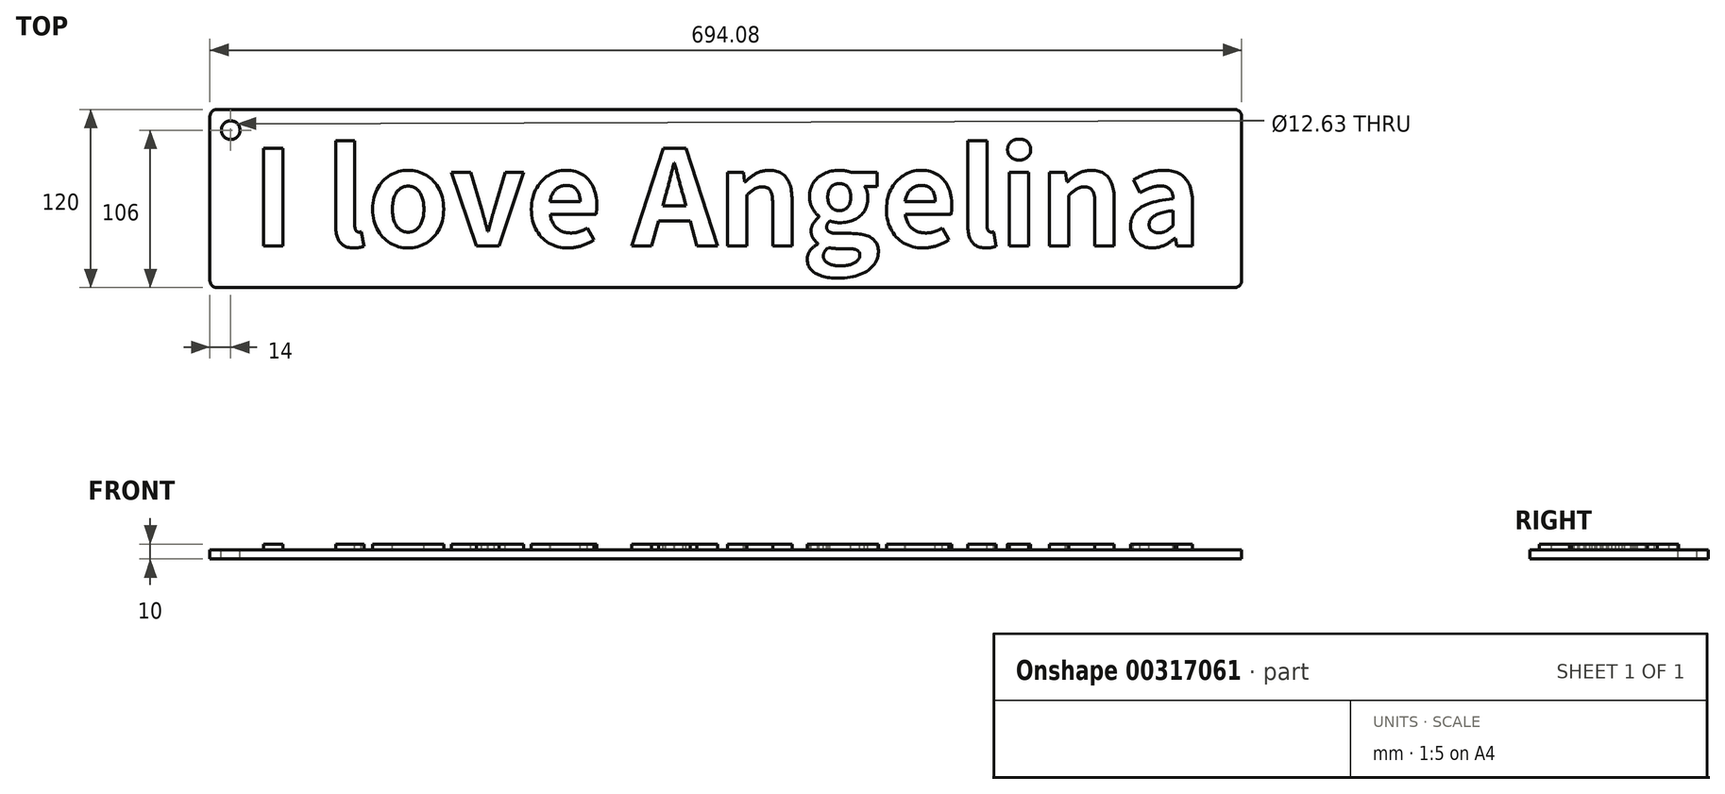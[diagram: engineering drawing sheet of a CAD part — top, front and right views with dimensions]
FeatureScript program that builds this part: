
annotation { "Feature Type Name" : "Feature", "Feature Type Description" : "" }
export const myFeature = defineFeature(function(context is Context, id is Id, definition is map)
    precondition{}
    {
        {
            var Q0;
            Q0=qCreatedBy(makeId("Top.planeOp"),FACE);
            var sketch = newSketch(context, id + "F0", { "sketchPlane" : qUnion([Q0])});
            skText(sketch, "E0", { "text": "I love Angelina\n", "fontName": "NotoSansCJKkr-Bold.otf"});
            skLineSegment(sketch, "E1.bottom", {"start": v(-23, -28) * mm, "end": v(661.08, -28) * mm});
            skLineSegment(sketch, "E1.top", {"start": v(-23, 92) * mm, "end": v(661.08, 92) * mm});
            skLineSegment(sketch, "E1.left", {"start": v(-28, -23) * mm, "end": v(-28, 87) * mm});
            skLineSegment(sketch, "E1.right", {"start": v(666.08, -23) * mm, "end": v(666.08, 87) * mm});
            skLineSegment(sketch, "E2", {"start": v(0, 64) * mm, "end": v(-28, 92) * mm});
            skLineSegment(sketch, "E3", {"start": v(-28, -28) * mm, "end": v(0, 0) * mm});
            skLineSegment(sketch, "E4", {"start": v(666.08, -28) * mm, "end": v(638.08, 0) * mm});
            skLineSegment(sketch, "E5", {"start": v(0, 64) * mm, "end": v(0, 92) * mm});
            skLineSegment(sketch, "E6", {"start": v(0, 0) * mm, "end": v(0, -28) * mm});
            skLineSegment(sketch, "E7", {"start": v(0, 64) * mm, "end": v(-28, 64) * mm});
            skPoint(sketch, "E8.visualSharp", {"position": v(-28, 92) * mm});
            skArc(sketch, "E8.filletArc", {"start": v(-23, 92) * mm, "mid": v(-26.54, 90.54) * mm, "end": v(-28, 87) * mm});
            skPoint(sketch, "E9.visualSharp", {"position": v(-28, -28) * mm});
            skArc(sketch, "E9.filletArc", {"start": v(-28, -23) * mm, "mid": v(-26.54, -26.54) * mm, "end": v(-23, -28) * mm});
            skPoint(sketch, "E10.visualSharp", {"position": v(666.08, -28) * mm});
            skArc(sketch, "E10.filletArc", {"start": v(661.08, -28) * mm, "mid": v(664.62, -26.54) * mm, "end": v(666.08, -23) * mm});
            skPoint(sketch, "E11.visualSharp", {"position": v(666.08, 92) * mm});
            skArc(sketch, "E11.filletArc", {"start": v(666.08, 87) * mm, "mid": v(664.62, 90.54) * mm, "end": v(661.08, 92) * mm});
            skPoint(sketch, "E12", {"position": v(-14, 78) * mm});
            skCircle(sketch, "E13", {"center": v(-14, 78) * mm, "radius": 6.31 * mm});
            const initialGuessF0  = {"E0": [0, 0, 1, 0, 0.064]};
            skSetInitialGuess(sketch, initialGuessF0);
            skSolve(sketch);
        }
        {
            var Q0;
            Q0 = qSketchRegion(id + "F0", true);
            var Q1;
            Q1=makeQuery(id+"F0.imprint","IMPRINT",FACE,{"disambiguationData":[TD([[makeQuery(id+"F0.imprint","IMPRINT",EDGE,{"derivedFrom":sQuery(id+"F0.wireOp",EDGE,"E0.sketch_text.stroke-12")}),1.0]])]});
            var Q2;
            Q2=makeQuery(id+"F0.imprint","IMPRINT",FACE,{"disambiguationData":[TD([[makeQuery(id+"F0.imprint","IMPRINT",EDGE,{"derivedFrom":sQuery(id+"F0.wireOp",EDGE,"E0.sketch_text.stroke-0")}),-1.0]])]});
            var Q3;
            Q3=makeQuery(id+"F0.imprint","IMPRINT",FACE,{"disambiguationData":[TD([[makeQuery(id+"F0.imprint","IMPRINT",EDGE,{"derivedFrom":sQuery(id+"F0.wireOp",EDGE,"E0.sketch_text.stroke-69")}),1.0]])]});
            var Q4;
            Q4=makeQuery(id+"F0.imprint","IMPRINT",FACE,{"disambiguationData":[TD([[makeQuery(id+"F0.imprint","IMPRINT",EDGE,{"derivedFrom":sQuery(id+"F0.wireOp",EDGE,"E0.sketch_text.stroke-123")}),1.0]])]});
            var Q5;
            Q5=makeQuery(id+"F0.imprint","IMPRINT",FACE,{"disambiguationData":[TD([[makeQuery(id+"F0.imprint","IMPRINT",EDGE,{"derivedFrom":sQuery(id+"F0.wireOp",EDGE,"E0.sketch_text.stroke-119")}),1.0]])]});
            var Q6;
            Q6=makeQuery(id+"F0.imprint","IMPRINT",FACE,{"disambiguationData":[TD([[makeQuery(id+"F0.imprint","IMPRINT",EDGE,{"derivedFrom":sQuery(id+"F0.wireOp",EDGE,"E0.sketch_text.stroke-108")}),-1.0]])]});
            var Q7;
            Q7=makeQuery(id+"F0.imprint","IMPRINT",FACE,{"disambiguationData":[TD([[makeQuery(id+"F0.imprint","IMPRINT",EDGE,{"derivedFrom":sQuery(id+"F0.wireOp",EDGE,"E0.sketch_text.stroke-93")}),-1.0]])]});
            var Q8;
            Q8=makeQuery(id+"F0.imprint","IMPRINT",FACE,{"disambiguationData":[TD([[makeQuery(id+"F0.imprint","IMPRINT",EDGE,{"derivedFrom":sQuery(id+"F0.wireOp",EDGE,"E0.sketch_text.stroke-89")}),-1.0]])]});
            var Q9;
            Q9=makeQuery(id+"F0.imprint","IMPRINT",FACE,{"disambiguationData":[TD([[makeQuery(id+"F0.imprint","IMPRINT",EDGE,{"derivedFrom":sQuery(id+"F0.wireOp",EDGE,"E0.sketch_text.stroke-56")}),1.0]])]});
            var Q10;
            Q10=makeQuery(id+"F0.imprint","IMPRINT",FACE,{"disambiguationData":[TD([[makeQuery(id+"F0.imprint","IMPRINT",EDGE,{"derivedFrom":sQuery(id+"F0.wireOp",EDGE,"E0.sketch_text.stroke-42")}),-1.0]])]});
            var Q11;
            Q11=makeQuery(id+"F0.imprint","IMPRINT",FACE,{"disambiguationData":[TD([[makeQuery(id+"F0.imprint","IMPRINT",EDGE,{"derivedFrom":sQuery(id+"F0.wireOp",EDGE,"E0.sketch_text.stroke-42")}),1.0]])]});
            var Q12;
            Q12=makeQuery(id+"F0.imprint","IMPRINT",FACE,{"disambiguationData":[TD([[makeQuery(id+"F0.imprint","IMPRINT",EDGE,{"derivedFrom":sQuery(id+"F0.wireOp",EDGE,"E0.sketch_text.stroke-39")}),-1.0]])]});
            var Q13;
            Q13=makeQuery(id+"F0.imprint","IMPRINT",FACE,{"disambiguationData":[TD([[makeQuery(id+"F0.imprint","IMPRINT",EDGE,{"derivedFrom":sQuery(id+"F0.wireOp",EDGE,"E0.sketch_text.stroke-20")}),1.0]])]});
            var Q14;
            Q14=makeQuery(id+"F0.imprint","IMPRINT",FACE,{"disambiguationData":[TD([[makeQuery(id+"F0.imprint","IMPRINT",EDGE,{"derivedFrom":sQuery(id+"F0.wireOp",EDGE,"E0.sketch_text.stroke-16")}),-1.0]])]});
            var Q15;
            Q15=makeQuery(id+"F0.imprint","IMPRINT",FACE,{"disambiguationData":[TD([[makeQuery(id+"F0.imprint","IMPRINT",EDGE,{"derivedFrom":sQuery(id+"F0.wireOp",EDGE,"E0.sketch_text.stroke-4")}),1.0]])]});
            var Q16;
            Q16=makeQuery(id+"F0.imprint","IMPRINT",FACE,{"disambiguationData":[TD([[makeQuery(id+"F0.imprint","IMPRINT",EDGE,{"derivedFrom":sQuery(id+"F0.wireOp",EDGE,"E0.sketch_text.stroke-0")}),1.0]])]});
            var Q17;
            Q17=makeQuery(id+"F0.imprint","IMPRINT",FACE,{"disambiguationData":[TD([[makeQuery(id+"F0.imprint","IMPRINT",EDGE,{"derivedFrom":sQuery(id+"F0.wireOp",EDGE,"E0.sketch_text.stroke-152")}),-1.0]])]});
            var Q18;
            Q18=makeQuery(id+"F0.imprint","IMPRINT",FACE,{"disambiguationData":[TD([[makeQuery(id+"F0.imprint","IMPRINT",EDGE,{"derivedFrom":sQuery(id+"F0.wireOp",EDGE,"E0.sketch_text.stroke-127")}),1.0]])]});
            var Q19;
            {var subQ3=sQuery(id+"F0.wireOp",EDGE,"E6");Q19=makeQuery(id+"F0.imprint","IMPRINT",FACE,{"disambiguationData":[TD([[makeQuery(id+"F0.imprint","IMPRINT",EDGE,{"derivedFrom":subQ3}),-1.0]])]});}
            var Q20;
            {var subQ3=sQuery(id+"F0.wireOp",EDGE,"E7");Q20=makeQuery(id+"F0.imprint","IMPRINT",FACE,{"disambiguationData":[TD([[makeQuery(id+"F0.imprint","IMPRINT",EDGE,{"derivedFrom":subQ3}),-1.0]])]});}
            var Q21;
            {var subQ3=sQuery(id+"F0.wireOp",EDGE,"E5");Q21=makeQuery(id+"F0.imprint","IMPRINT",FACE,{"disambiguationData":[TD([[makeQuery(id+"F0.imprint","IMPRINT",EDGE,{"derivedFrom":subQ3}),1.0]])]});}
            var Q22;
            Q22=makeQuery(id+"F0.imprint","IMPRINT",FACE,{"disambiguationData":[TD([[makeQuery(id+"F0.imprint","IMPRINT",EDGE,{"derivedFrom":sQuery(id+"F0.wireOp",EDGE,"E0.sketch_text.stroke-99")}),1.0]])]});
            var Q23;
            Q23=makeQuery(id+"F0.imprint","IMPRINT",FACE,{"disambiguationData":[TD([[makeQuery(id+"F0.imprint","IMPRINT",EDGE,{"derivedFrom":sQuery(id+"F0.wireOp",EDGE,"E0.sketch_text.stroke-140")}),1.0]])]});
            var Q24;
            Q24=makeQuery(id+"F0.imprint","IMPRINT",FACE,{"disambiguationData":[TD([[makeQuery(id+"F0.imprint","IMPRINT",EDGE,{"derivedFrom":sQuery(id+"F0.wireOp",EDGE,"E0.sketch_text.stroke-30")}),1.0]])]});
            var Q25;
            Q25=makeQuery(id+"F0.imprint","IMPRINT",FACE,{"disambiguationData":[TD([[makeQuery(id+"F0.imprint","IMPRINT",EDGE,{"derivedFrom":sQuery(id+"F0.wireOp",EDGE,"E0.sketch_text.stroke-111")}),1.0]])]});
            extrude(context, id + "F1", {"entities" : qUnion([Q0, Q1, Q2, Q3, Q4, Q5, Q6, Q7, Q8, Q9, Q10, Q11, Q12, Q13, Q14, Q15, Q16, Q17, Q18, Q19, Q20, Q21, Q22, Q23, Q24, Q25]), "oppositeDirection" : true, "depth" : 10 * mm});
        }
        {
            var Q0;
            Q0=makeQuery(id+"F0.imprint","IMPRINT",FACE,{"disambiguationData":[TD([[makeQuery(id+"F0.imprint","IMPRINT",EDGE,{"derivedFrom":sQuery(id+"F0.wireOp",EDGE,"E0.sketch_text.stroke-0")}),-1.0]])]});
            var Q1;
            Q1=makeQuery(id+"F0.imprint","IMPRINT",FACE,{"disambiguationData":[TD([[makeQuery(id+"F0.imprint","IMPRINT",EDGE,{"derivedFrom":sQuery(id+"F0.wireOp",EDGE,"E0.sketch_text.stroke-39")}),-1.0]])]});
            var Q2;
            Q2=makeQuery(id+"F0.imprint","IMPRINT",FACE,{"disambiguationData":[TD([[makeQuery(id+"F0.imprint","IMPRINT",EDGE,{"derivedFrom":sQuery(id+"F0.wireOp",EDGE,"E0.sketch_text.stroke-42")}),-1.0]])]});
            var Q3;
            Q3=makeQuery(id+"F0.imprint","IMPRINT",FACE,{"disambiguationData":[TD([[makeQuery(id+"F0.imprint","IMPRINT",EDGE,{"derivedFrom":sQuery(id+"F0.wireOp",EDGE,"E0.sketch_text.stroke-16")}),-1.0]])]});
            var Q4;
            Q4=makeQuery(id+"F0.imprint","IMPRINT",FACE,{"disambiguationData":[TD([[makeQuery(id+"F0.imprint","IMPRINT",EDGE,{"derivedFrom":sQuery(id+"F0.wireOp",EDGE,"E0.sketch_text.stroke-89")}),-1.0]])]});
            var Q5;
            Q5=makeQuery(id+"F0.imprint","IMPRINT",FACE,{"disambiguationData":[TD([[makeQuery(id+"F0.imprint","IMPRINT",EDGE,{"derivedFrom":sQuery(id+"F0.wireOp",EDGE,"E0.sketch_text.stroke-93")}),-1.0]])]});
            var Q6;
            Q6=makeQuery(id+"F0.imprint","IMPRINT",FACE,{"disambiguationData":[TD([[makeQuery(id+"F0.imprint","IMPRINT",EDGE,{"derivedFrom":sQuery(id+"F0.wireOp",EDGE,"E0.sketch_text.stroke-108")}),-1.0]])]});
            var Q7;
            Q7=makeQuery(id+"F0.imprint","IMPRINT",FACE,{"disambiguationData":[TD([[makeQuery(id+"F0.imprint","IMPRINT",EDGE,{"derivedFrom":sQuery(id+"F0.wireOp",EDGE,"E0.sketch_text.stroke-152")}),-1.0]])]});
            var Q8;
            {var subQ3=sQuery(id+"F0.wireOp",EDGE,"E7");Q8=makeQuery(id+"F0.imprint","IMPRINT",FACE,{"disambiguationData":[TD([[makeQuery(id+"F0.imprint","IMPRINT",EDGE,{"derivedFrom":subQ3}),-1.0]])]});}
            var Q9;
            {var subQ3=sQuery(id+"F0.wireOp",EDGE,"E5");Q9=makeQuery(id+"F0.imprint","IMPRINT",FACE,{"disambiguationData":[TD([[makeQuery(id+"F0.imprint","IMPRINT",EDGE,{"derivedFrom":subQ3}),1.0]])]});}
            var Q10;
            {var subQ3=sQuery(id+"F0.wireOp",EDGE,"E6");Q10=makeQuery(id+"F0.imprint","IMPRINT",FACE,{"disambiguationData":[TD([[makeQuery(id+"F0.imprint","IMPRINT",EDGE,{"derivedFrom":subQ3}),-1.0]])]});}
            extrude(context, id + "F2", {"entities" : qUnion([Q0, Q1, Q2, Q3, Q4, Q5, Q6, Q7, Q8, Q9, Q10]), "operationType" : NewBodyOperationType.REMOVE, "oppositeDirection" : true, "depth" : 4 * mm});
        }
    });
